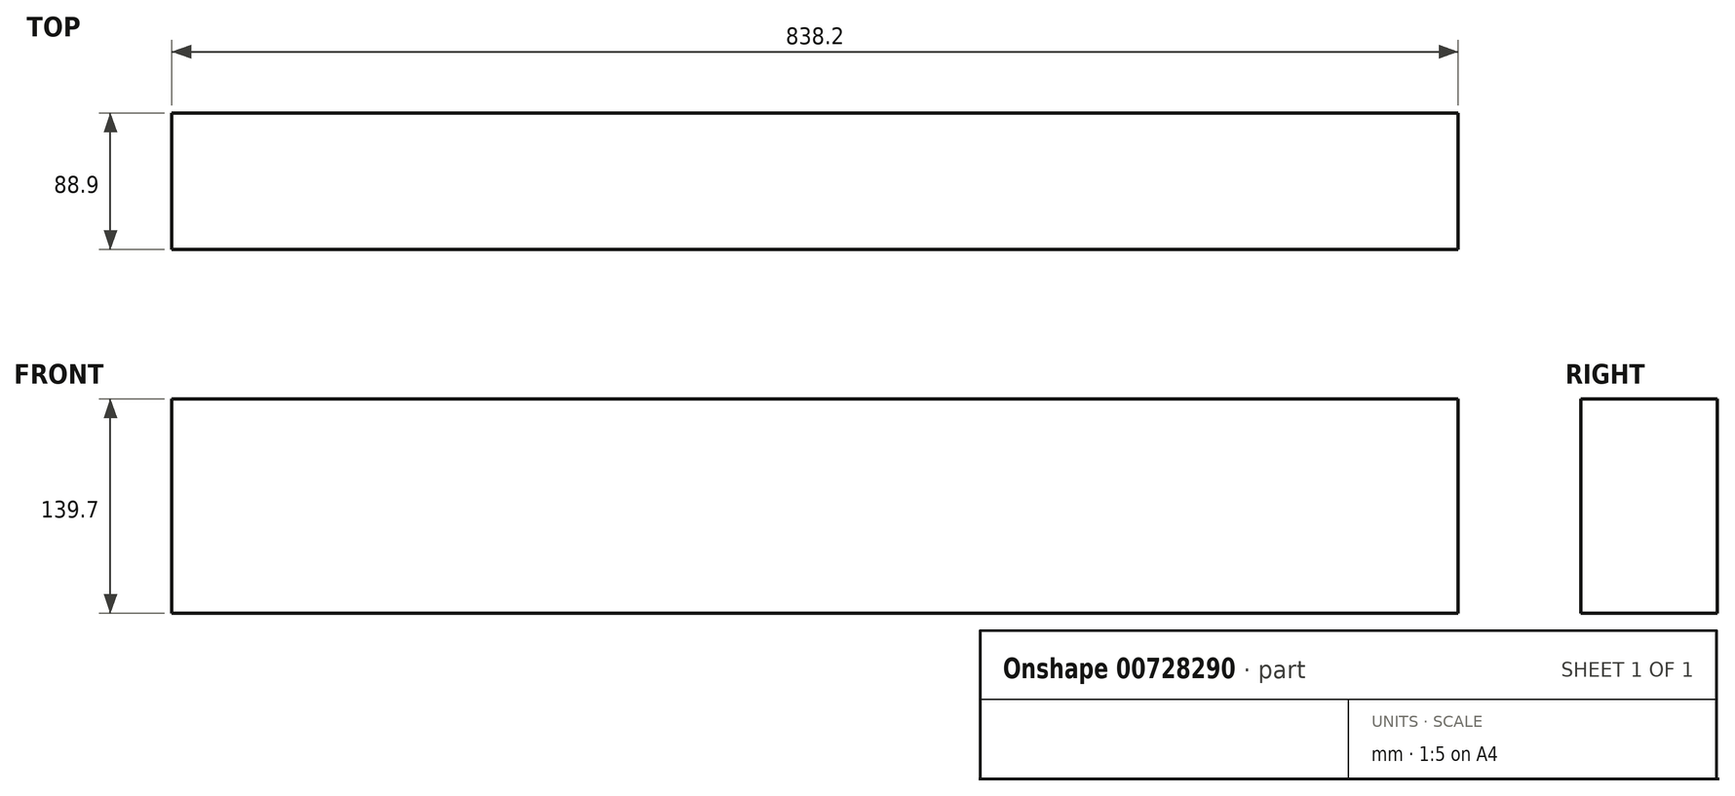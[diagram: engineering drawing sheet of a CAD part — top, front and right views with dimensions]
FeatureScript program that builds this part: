
annotation { "Feature Type Name" : "Feature", "Feature Type Description" : "" }
export const myFeature = defineFeature(function(context is Context, id is Id, definition is map)
    precondition{}
    {
        {
            var Q0;
            Q0=qCreatedBy(makeId("Front.planeOp"),FACE);
            var sketch = newSketch(context, id + "F0", { "sketchPlane" : qUnion([Q0])});
            skLineSegment(sketch, "E0.bottom", {"start": v(-419.1, -69.85) * mm, "end": v(419.1, -69.85) * mm});
            skLineSegment(sketch, "E0.top", {"start": v(-419.1, 69.85) * mm, "end": v(419.1, 69.85) * mm});
            skLineSegment(sketch, "E0.left", {"start": v(-419.1, -69.85) * mm, "end": v(-419.1, 69.85) * mm});
            skLineSegment(sketch, "E0.right", {"start": v(419.1, -69.85) * mm, "end": v(419.1, 69.85) * mm});
            skPoint(sketch, "E0.middle", {"position": v(0, 0) * mm});
            skSolve(sketch);
        }
        {
            var Q0;
            Q0=makeQuery(id+"F0.imprint","IMPRINT",FACE,{"disambiguationData":[TD([[makeQuery(id+"F0.imprint","IMPRINT",EDGE,{"derivedFrom":sQuery(id+"F0.wireOp",EDGE,"E0.bottom")}),1.0]])]});
            extrude(context, id + "F1", {"entities" : qUnion([Q0]), "depth" : 88.9 * mm, "offsetDistance" : 25.4 * mm});
        }
    });
